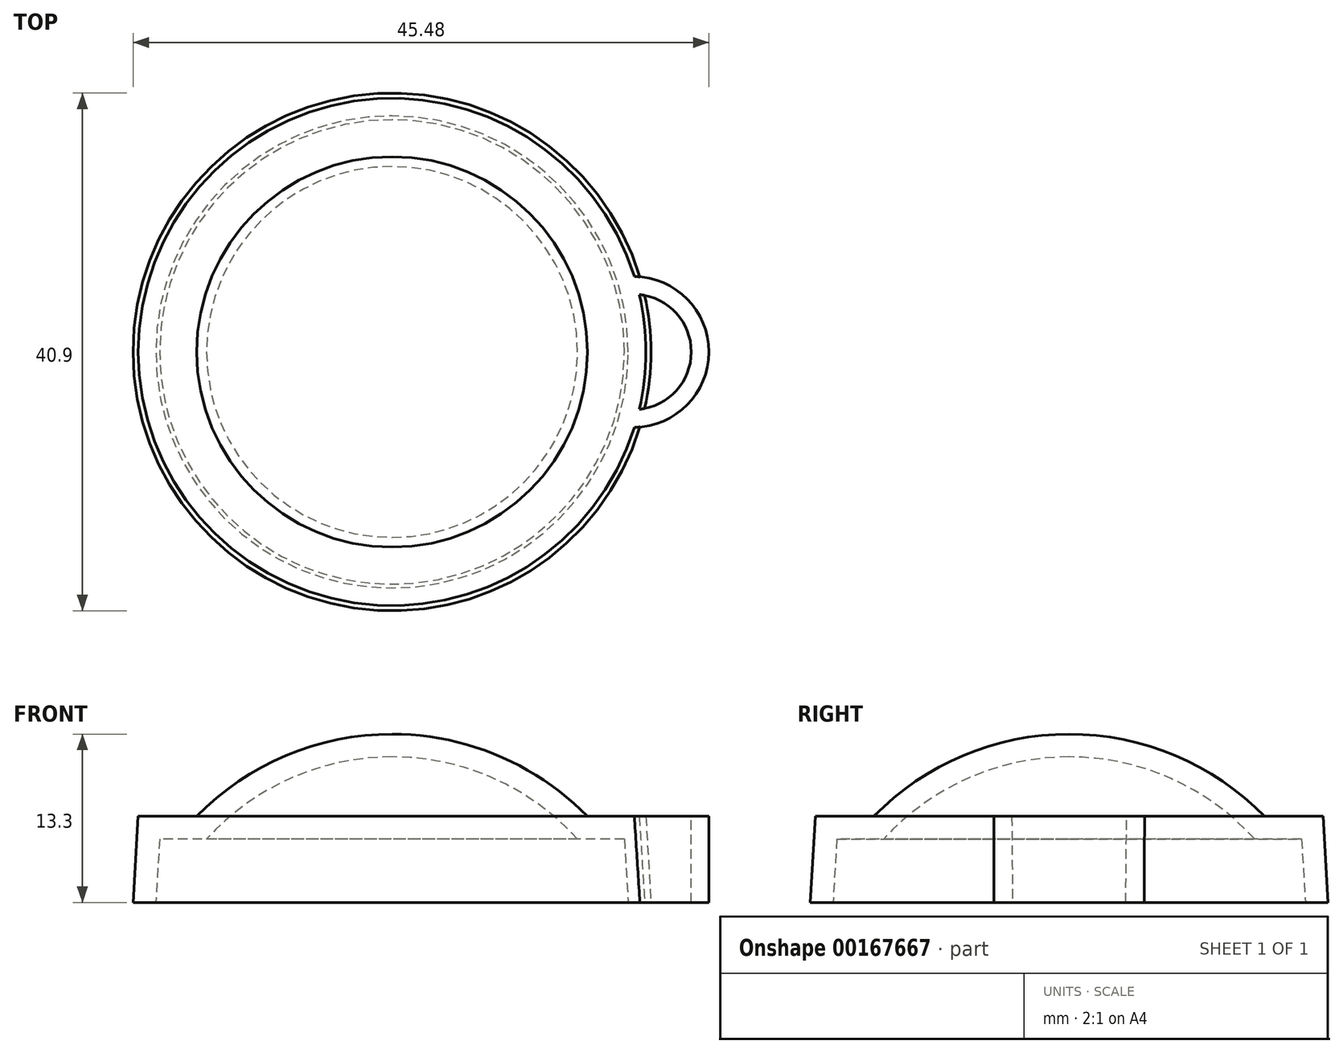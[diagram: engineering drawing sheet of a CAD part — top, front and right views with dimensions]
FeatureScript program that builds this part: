
annotation { "Feature Type Name" : "Feature", "Feature Type Description" : "" }
export const myFeature = defineFeature(function(context is Context, id is Id, definition is map)
    precondition{}
    {
        {
            var Q0;
            Q0=qCreatedBy(makeId("Front.planeOp"),FACE);
            var sketch = newSketch(context, id + "F0", { "sketchPlane" : qUnion([Q0])});
            skLineSegment(sketch, "E0", {"start": v(0, 0) * mm, "end": v(18.65, 0) * mm});
            skLineSegment(sketch, "E1", {"start": v(18.65, 5) * mm, "end": v(14.65, 5) * mm});
            skLineSegment(sketch, "E2", {"start": v(18.65, 0) * mm, "end": v(18.65, 5) * mm});
            skCircle(sketch, "E3", {"center": v(0, -8.26) * mm, "radius": 19.76 * mm});
            skLineSegment(sketch, "E4", {"start": v(0, 11.5) * mm, "end": v(0, 0) * mm});
            skLineSegment(sketch, "E5", {"start": v(18.35, 5) * mm, "end": v(18.65, 0) * mm});
            skSolve(sketch);
        }
        {
            var Q0;
            {var subQ0=sQuery(id+"F0.wireOp",EDGE,"E4");Q0=makeQuery(id+"F0.imprint","IMPRINT",FACE,{"disambiguationData":[TD([[makeQuery(id+"F0.imprint","IMPRINT",EDGE,{"derivedFrom":subQ0}),1.0]])]});}
            var Q1;
            {var subQ0=sQuery(id+"F0.wireOp",EDGE,"E5");Q1=makeQuery(id+"F0.imprint","IMPRINT",FACE,{"disambiguationData":[TD([[makeQuery(id+"F0.imprint","IMPRINT",EDGE,{"derivedFrom":subQ0}),-1.0]])]});}
            var Q2;
            Q2=sQuery(id+"F0.wireOp",EDGE,"E4");
            revolve(context, id + "F1", {"entities" : qUnion([Q0, Q1]), "axis" : qUnion([Q2]), "revolveType" : RevolveType.FULL});
        }
        {
            var Q0;
            Q0=makeQuery(id+"F1.opRevolve","SWEPT_FACE",FACE,{"disambiguationData":[OSD([sQuery(id+"F0.wireOp",EDGE,"E0")])]});
            shell(context, id + "F2", {"entities" : qUnion([Q0]), "thickness" : 1.8 * mm, "oppositeDirection" : true});
        }
        {
            var Q0;
            Q0=makeQuery(id+"F1.opRevolve","SWEPT_FACE",FACE,{"disambiguationData":[OSD([sQuery(id+"F0.wireOp",EDGE,"E1")])]});
            var sketch = newSketch(context, id + "F3", { "sketchPlane" : qUnion([Q0])});
            skCircle(sketch, "E6", {"center": v(19.08, 0) * mm, "radius": 4.55 * mm});
            skCircle(sketch, "E7", {"center": v(19.08, 0) * mm, "radius": 5.95 * mm});
            skCircle(sketch, "E8.0", {"center": v(0, 0) * mm, "radius": 15.43 * mm});
            skSolve(sketch);
        }
        {
            var Q0;
            {var subQ0=sQuery(id+"F3.wireOp",EDGE,"E6");var subQ1=makeQuery(id+"F1.opRevolve","SWEPT_EDGE",EDGE,{"disambiguationData":[OSD([sQuery(id+"F0.wireOp",EDGE,"E1"),sQuery(id+"F0.wireOp",EDGE,"E5")])]});var subQ2=makeQuery(id+"F3.imprint","INTERSECT",VERTEX,{"disambiguationData":[OD(0.0)],"derivedFrom":[subQ1,subQ0]});Q0=makeQuery(id+"F3.imprint","IMPRINT",FACE,{"disambiguationData":[TD([[makeQuery(id+"F3.imprint","IMPRINT",EDGE,{"disambiguationData":[TD([[subQ2,1.0]])],"derivedFrom":subQ0}),-1.0]])]});}
            var Q1;
            Q1=makeQuery(id+"F1.opRevolve","SWEPT_FACE",FACE,{"disambiguationData":[OSD([sQuery(id+"F0.wireOp",EDGE,"E0")])]});
            extrude(context, id + "F4", {"entities" : qUnion([Q0]), "operationType" : NewBodyOperationType.ADD, "endBound" : BoundingType.UP_TO_SURFACE, "oppositeDirection" : true, "endBoundEntityFace" : qUnion([Q1]), "depth" : 4 * mm});
        }
    });
